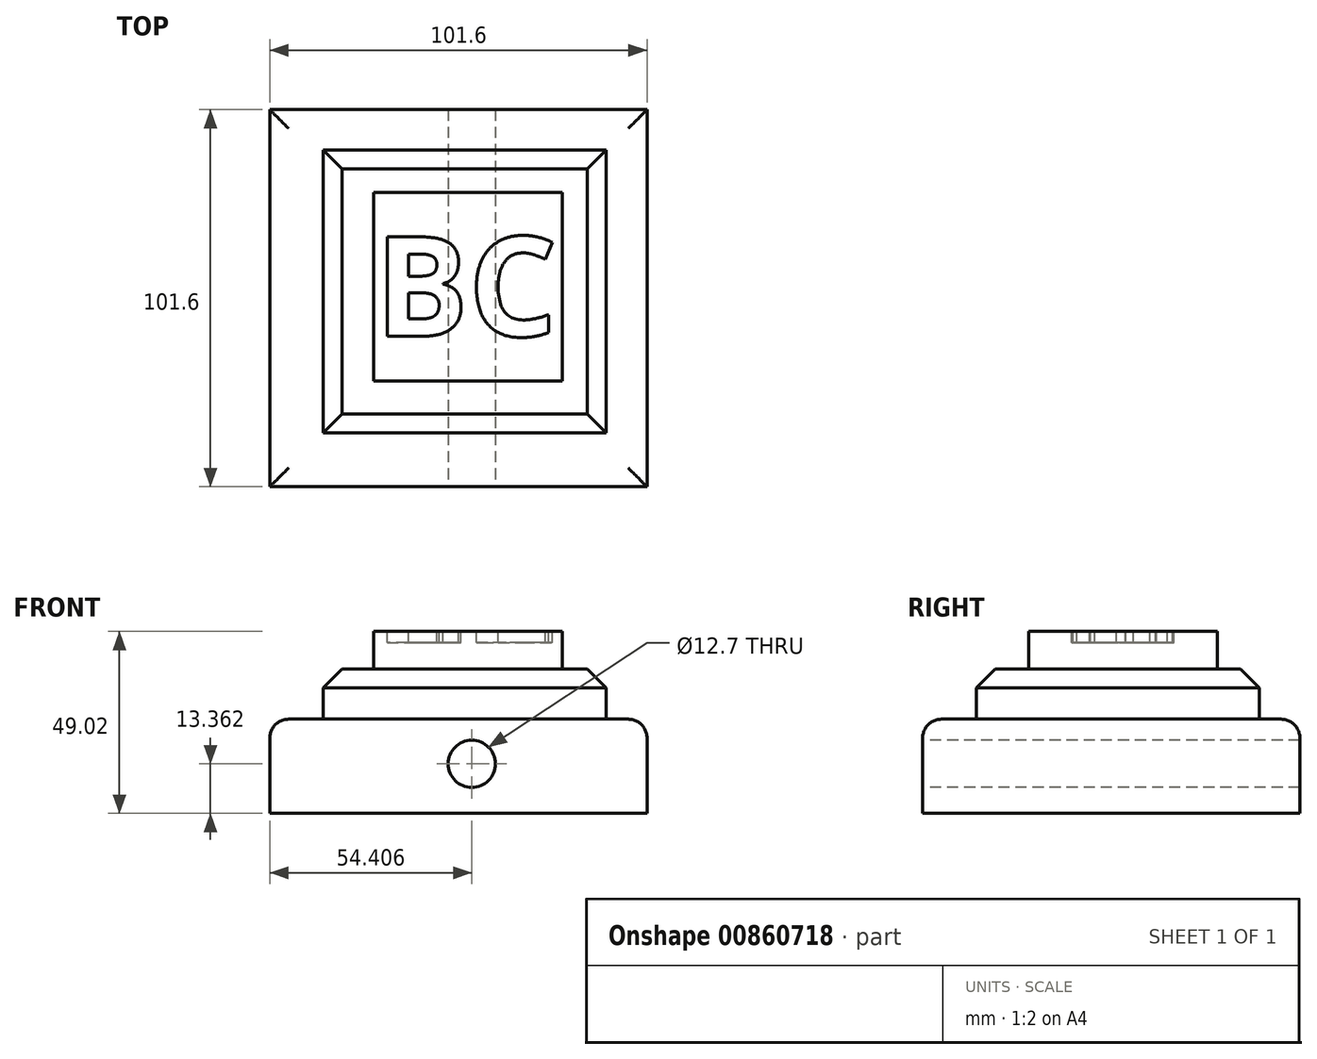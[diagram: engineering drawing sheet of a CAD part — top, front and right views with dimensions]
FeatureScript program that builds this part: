
annotation { "Feature Type Name" : "Feature", "Feature Type Description" : "" }
export const myFeature = defineFeature(function(context is Context, id is Id, definition is map)
    precondition{}
    {
        {
            var Q0;
            Q0=qCreatedBy(makeId("Top.planeOp"),FACE);
            var sketch = newSketch(context, id + "F0", { "sketchPlane" : qUnion([Q0])});
            skLineSegment(sketch, "E0.bottom", {"start": v(0, 0) * mm, "end": v(101.6, 0) * mm});
            skLineSegment(sketch, "E0.top", {"start": v(0, 101.6) * mm, "end": v(101.6, 101.6) * mm});
            skLineSegment(sketch, "E0.left", {"start": v(0, 0) * mm, "end": v(0, 101.6) * mm});
            skLineSegment(sketch, "E0.right", {"start": v(101.6, 0) * mm, "end": v(101.6, 101.6) * mm});
            skSolve(sketch);
        }
        {
            var Q0;
            Q0=makeQuery(id+"F0.imprint","IMPRINT",FACE,{"disambiguationData":[TD([[makeQuery(id+"F0.imprint","IMPRINT",EDGE,{"derivedFrom":sQuery(id+"F0.wireOp",EDGE,"E0.bottom")}),1.0]])]});
            extrude(context, id + "F1", {"entities" : qUnion([Q0]), "depth" : 25.4 * mm, "offsetDistance" : 25.4 * mm});
        }
        {
            var Q0;
            Q0=qCreatedBy(makeId("Top.planeOp"),FACE);
            var sketch = newSketch(context, id + "F2", { "sketchPlane" : qUnion([Q0])});
            skLineSegment(sketch, "E1.bottom", {"start": v(14.42, 14.47) * mm, "end": v(90.62, 14.47) * mm});
            skLineSegment(sketch, "E1.top", {"start": v(14.42, 90.67) * mm, "end": v(90.62, 90.67) * mm});
            skLineSegment(sketch, "E1.left", {"start": v(14.42, 14.47) * mm, "end": v(14.42, 90.67) * mm});
            skLineSegment(sketch, "E1.right", {"start": v(90.62, 14.47) * mm, "end": v(90.62, 90.67) * mm});
            skSolve(sketch);
        }
        {
            var Q0;
            Q0 = qSketchRegion(id + "F2", true);
            extrude(context, id + "F3", {"entities" : qUnion([Q0]), "operationType" : NewBodyOperationType.ADD, "depth" : 38.86 * mm, "offsetDistance" : 25.4 * mm});
        }
        {
            var Q0;
            Q0=qCreatedBy(makeId("Top.planeOp"),FACE);
            var sketch = newSketch(context, id + "F4", { "sketchPlane" : qUnion([Q0])});
            skLineSegment(sketch, "E2.bottom", {"start": v(28.02, 28.54) * mm, "end": v(78.82, 28.54) * mm});
            skLineSegment(sketch, "E2.top", {"start": v(28.02, 79.34) * mm, "end": v(78.82, 79.34) * mm});
            skLineSegment(sketch, "E2.left", {"start": v(28.02, 28.54) * mm, "end": v(28.02, 79.34) * mm});
            skLineSegment(sketch, "E2.right", {"start": v(78.82, 28.54) * mm, "end": v(78.82, 79.34) * mm});
            skSolve(sketch);
        }
        {
            var Q0;
            Q0 = qSketchRegion(id + "F4", true);
            extrude(context, id + "F5", {"entities" : qUnion([Q0]), "operationType" : NewBodyOperationType.ADD, "depth" : 49.02 * mm, "offsetDistance" : 25.4 * mm});
        }
        {
            var Q0;
            Q0=qCreatedBy(makeId("Front.planeOp"),FACE);
            var sketch = newSketch(context, id + "F6", { "sketchPlane" : qUnion([Q0])});
            skCircle(sketch, "E3", {"center": v(54.4, 13.36) * mm, "radius": 6.35 * mm});
            skSolve(sketch);
        }
        {
            var Q0;
            Q0 = qSketchRegion(id + "F6", true);
            extrude(context, id + "F7", {"entities" : qUnion([Q0]), "operationType" : NewBodyOperationType.REMOVE, "oppositeDirection" : true, "depth" : 154.43 * mm, "offsetDistance" : 25.4 * mm});
        }
        {
            var Q0;
            Q0=makeQuery(id+"F3.opExtrude","CAP_EDGE",EDGE,{"disambiguationData":[OSD([sQuery(id+"F2.wireOp",EDGE,"E1.right")])],"isStart":false});
            var Q1;
            Q1=makeQuery(id+"F3.opExtrude","CAP_EDGE",EDGE,{"disambiguationData":[OSD([sQuery(id+"F2.wireOp",EDGE,"E1.bottom")])],"isStart":false});
            var Q2;
            Q2=makeQuery(id+"F3.opExtrude","CAP_EDGE",EDGE,{"disambiguationData":[OSD([sQuery(id+"F2.wireOp",EDGE,"E1.left")])],"isStart":false});
            var Q3;
            Q3=makeQuery(id+"F3.opExtrude","CAP_EDGE",EDGE,{"disambiguationData":[OSD([sQuery(id+"F2.wireOp",EDGE,"E1.top")])],"isStart":false});
            chamfer(context, id + "F8", {"entities" : qUnion([Q0, Q1, Q2, Q3]), "width" : 5.08 * mm, "tangentPropagation" : true});
        }
        {
            var Q0;
            Q0=makeQuery(id+"F1.opExtrude","CAP_EDGE",EDGE,{"disambiguationData":[OSD([sQuery(id+"F0.wireOp",EDGE,"E0.bottom")])],"isStart":false});
            var Q1;
            Q1=makeQuery(id+"F1.opExtrude","CAP_EDGE",EDGE,{"disambiguationData":[OSD([sQuery(id+"F0.wireOp",EDGE,"E0.left")])],"isStart":false});
            var Q2;
            Q2=makeQuery(id+"F1.opExtrude","CAP_EDGE",EDGE,{"disambiguationData":[OSD([sQuery(id+"F0.wireOp",EDGE,"E0.right")])],"isStart":false});
            var Q3;
            Q3=makeQuery(id+"F1.opExtrude","CAP_EDGE",EDGE,{"disambiguationData":[OSD([sQuery(id+"F0.wireOp",EDGE,"E0.top")])],"isStart":false});
            fillet(context, id + "F9", {"entities" : qUnion([Q0, Q1, Q2, Q3]), "radius" : 5.08 * mm, "tangentPropagation" : true, "allowEdgeOverflow" : false});
        }
        {
            var Q0;
            Q0=makeQuery(id+"F5.opExtrude","CAP_FACE",FACE,{"disambiguationData":[OSD([sQuery(id+"F4.wireOp",EDGE,"E2.bottom"),sQuery(id+"F4.wireOp",EDGE,"E2.top"),sQuery(id+"F4.wireOp",EDGE,"E2.left"),sQuery(id+"F4.wireOp",EDGE,"E2.right")])],"isStart":false});
            var sketch = newSketch(context, id + "F10", { "sketchPlane" : qUnion([Q0])});
            skText(sketch, "E4", { "text": "BC", "fontName": "OpenSans-Bold.ttf"});
            const initialGuessF10  = {"E4": [0.02827, 0.04057, 1, 0, 0.02702]};
            skSetInitialGuess(sketch, initialGuessF10);
            skSolve(sketch);
        }
        {
            var Q0;
            Q0 = qSketchRegion(id + "F10", true);
            extrude(context, id + "F11", {"entities" : qUnion([Q0]), "operationType" : NewBodyOperationType.REMOVE, "oppositeDirection" : true, "depth" : 3.05 * mm, "offsetDistance" : 25.4 * mm});
        }
    });
